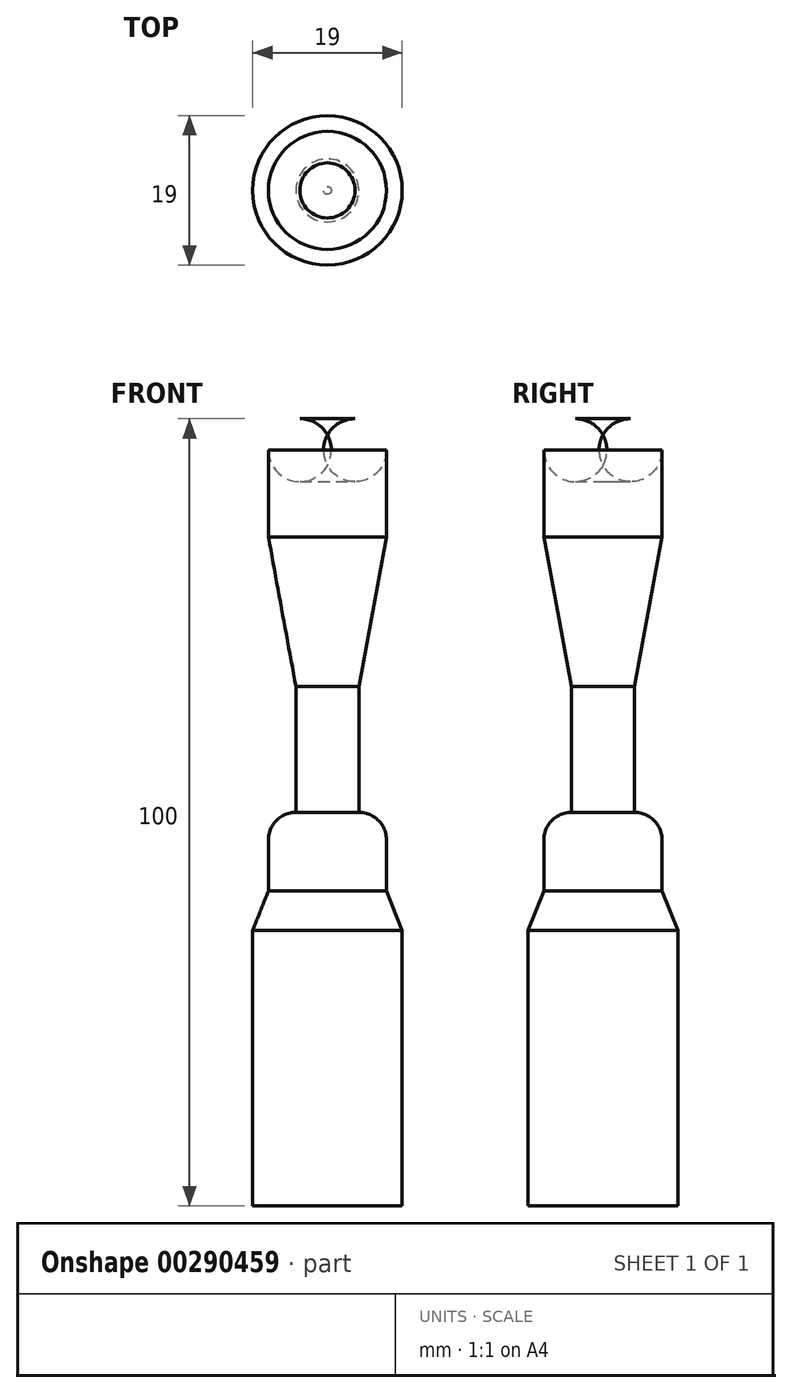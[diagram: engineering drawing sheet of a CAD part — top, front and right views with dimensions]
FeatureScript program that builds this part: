
annotation { "Feature Type Name" : "Feature", "Feature Type Description" : "" }
export const myFeature = defineFeature(function(context is Context, id is Id, definition is map)
    precondition{}
    {
        {
            var Q0;
            Q0=qCreatedBy(makeId("Front.planeOp"),FACE);
            var sketch = newSketch(context, id + "F0", { "sketchPlane" : qUnion([Q0])});
            skLineSegment(sketch, "E0", {"start": v(7.5, -4) * mm, "end": v(7.5, -15) * mm});
            skLineSegment(sketch, "E1", {"start": v(7.5, -15) * mm, "end": v(4, -34) * mm});
            skLineSegment(sketch, "E2", {"start": v(4, -34) * mm, "end": v(4, -50) * mm});
            skLineSegment(sketch, "E3", {"start": v(7.5, -53.5) * mm, "end": v(7.5, -60) * mm});
            skLineSegment(sketch, "E4", {"start": v(7.5, -60) * mm, "end": v(9.5, -65) * mm});
            skLineSegment(sketch, "E5", {"start": v(9.5, -65) * mm, "end": v(9.5, -100) * mm});
            skLineSegment(sketch, "E6", {"start": v(9.5, -100) * mm, "end": v(0, -100) * mm});
            skLineSegment(sketch, "E7", {"start": v(0, -100) * mm, "end": v(0, 0) * mm});
            skLineSegment(sketch, "E8", {"start": v(0, 0) * mm, "end": v(3.5, 0) * mm});
            skArc(sketch, "E9", {"start": v(7.5, -4) * mm, "mid": v(6.33, -1.17) * mm, "end": v(3.5, 0) * mm});
            skArc(sketch, "E10", {"start": v(7.5, -53.5) * mm, "mid": v(6.47, -51.03) * mm, "end": v(4, -50) * mm});
            skSolve(sketch);
        }
        {
            var Q0;
            Q0=makeQuery(id+"F0.imprint","IMPRINT",FACE,{"disambiguationData":[TD([[makeQuery(id+"F0.imprint","IMPRINT",EDGE,{"derivedFrom":sQuery(id+"F0.wireOp",EDGE,"E0")}),-1.0]])]});
            var Q1;
            Q1=sQuery(id+"F0.wireOp",EDGE,"E7");
            revolve(context, id + "F1", {"entities" : qUnion([Q0]), "axis" : qUnion([Q1]), "revolveType" : RevolveType.FULL});
        }
    });
